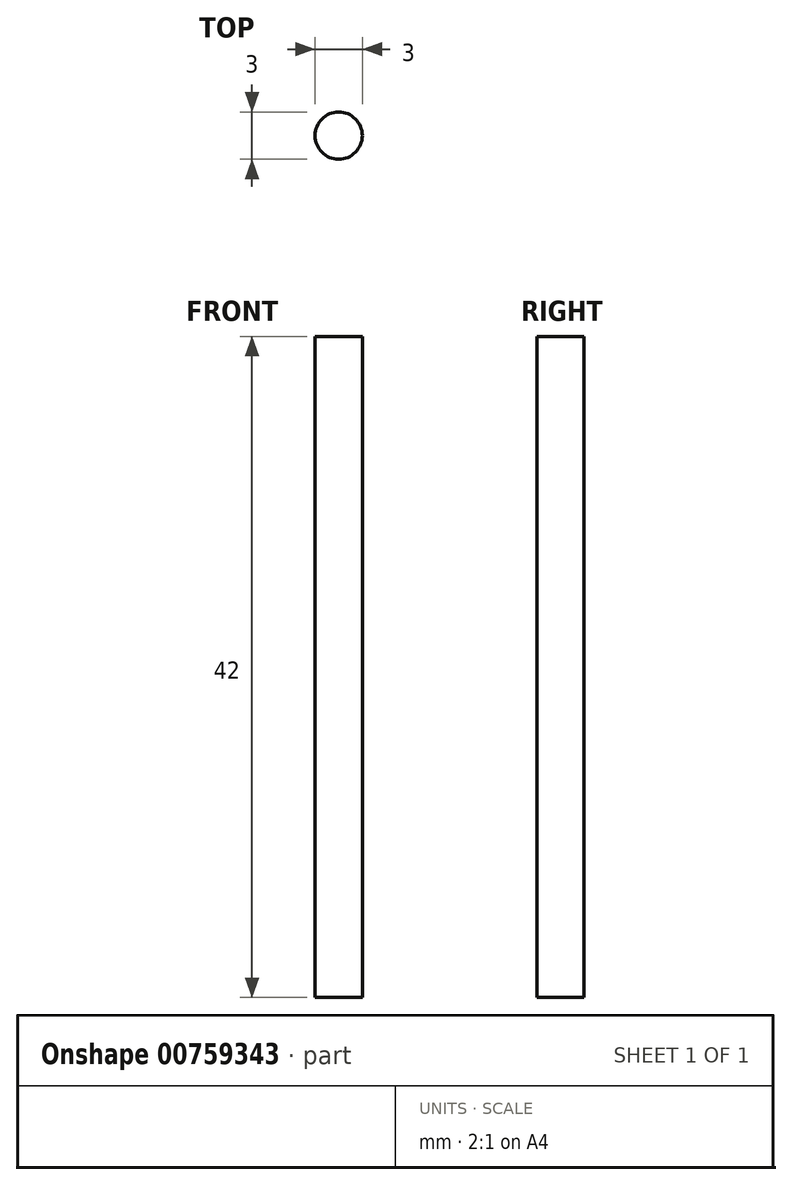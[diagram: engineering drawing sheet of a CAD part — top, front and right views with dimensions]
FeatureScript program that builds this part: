
annotation { "Feature Type Name" : "Feature", "Feature Type Description" : "" }
export const myFeature = defineFeature(function(context is Context, id is Id, definition is map)
    precondition{}
    {
        {
            var Q0;
            Q0=qCreatedBy(makeId("Top.planeOp"),FACE);
            var sketch = newSketch(context, id + "F0", { "sketchPlane" : qUnion([Q0])});
            skCircle(sketch, "E0", {"center": v(0, 0) * mm, "radius": 1.5 * mm});
            skSolve(sketch);
        }
        {
            var Q0;
            Q0=sQuery(id+"F0.wireOp",EDGE,"E0");
            extrude(context, id + "F1", {"bodyType" : ToolBodyType.SURFACE, "surfaceEntities" : qUnion([Q0]), "depth" : 42 * mm, "offsetDistance" : 25 * mm});
        }
    });
